# Revit family: ALMA-Hazel_Concealed_Hook_Pull_Handle
name_source: partatom
category: Specialty Equipment
units: mm (PartAtom-declared; Revit-internal decimal feet)

## family parameters
Cut with Voids When Loaded = Yes
Enable Cutting in Views = Yes
Host = Face
Maintain Annotation Orientation = No
Part Type = Normal
Room Calculation Point = No
Round Connector Dimension = Use Diameter
Shared = No

## types (5) — shared parameters
Default Elevation = 1219 mm
Depth = 15 mm
Length = 90 mm  [stored 0.295276 ft]
Width = 19 mm

## per-type parameters (varying)
| type | Material |
| BRUSHED VINTAGE ANTIQUE BRASS (DCHPVB05) | BM_ANTIQUE BRASS |
| BRUSHED NICKEL (DCHPBN04) | BM_NICKEL |
| BRUSHED BRASS GOLD (DCHPGD02) | BM_BRASS GOLD |
| BRUSHED GUNMETAL (DCHPGM03) | BM_GUNMETAL |
| MATTE BLACK (DCHPMB01) | BM_MATTE BLACK |

note: [stored X ft] marks values corroborated as IEEE doubles in the binary element streams (Revit-internal decimal feet)

## geometry (parser evidence)
native form markers: Sweep x1
no freeform markers — native parametric forms only
